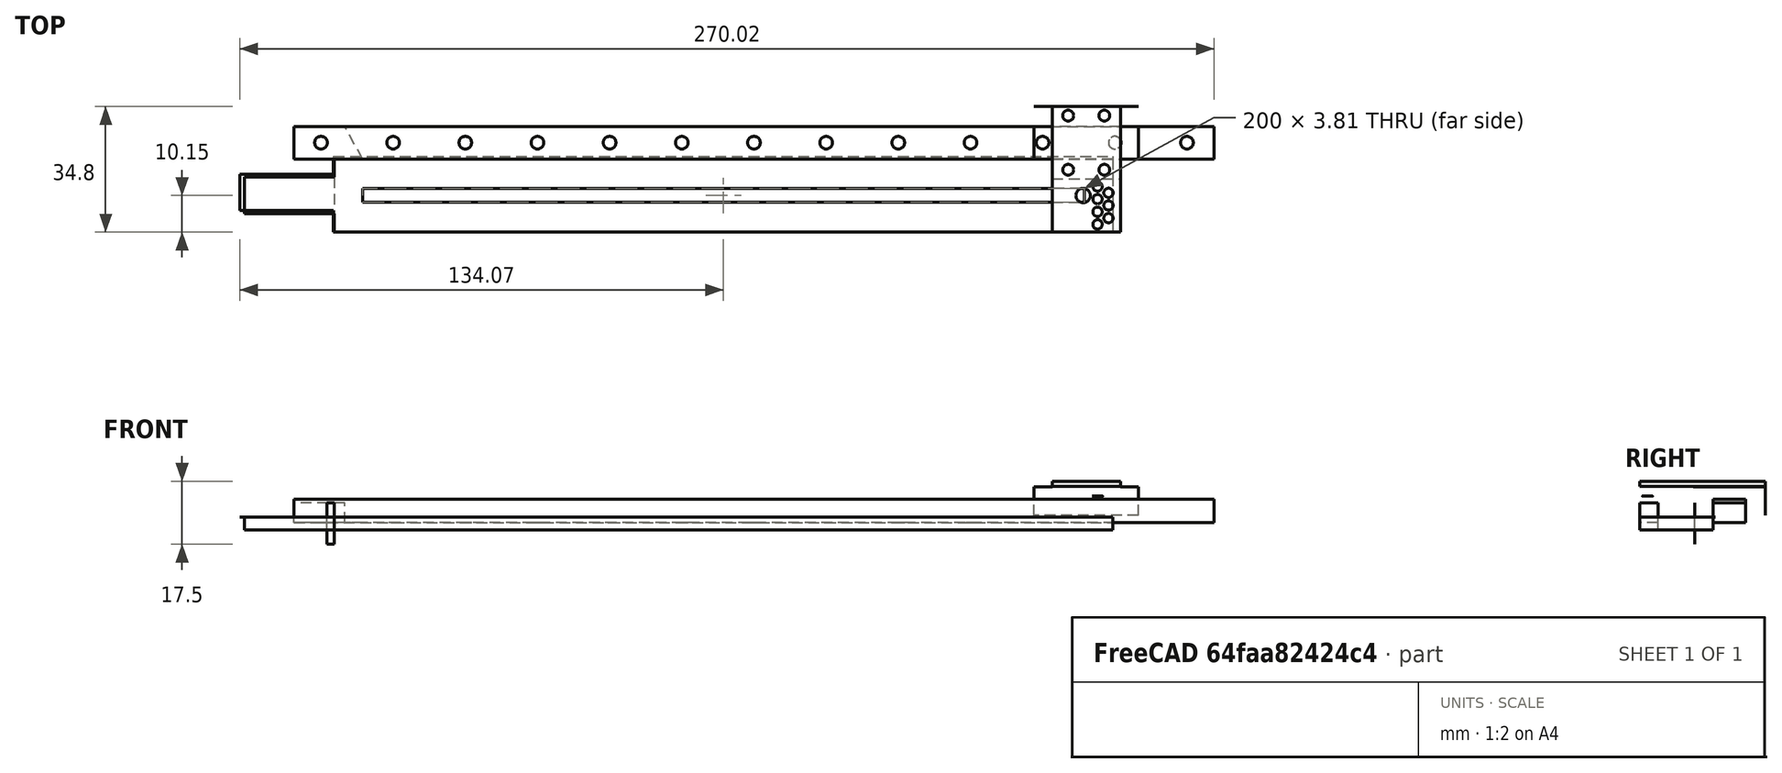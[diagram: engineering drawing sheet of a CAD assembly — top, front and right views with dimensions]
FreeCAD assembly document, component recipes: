
FREECAD ASSEMBLY — COMPONENT RECIPES ("v9")

This assembly document has 13 components, labeled P0..P12 below (a component is one placed body or linked part). 9 of them carry a construction recipe — the FreeCAD feature program that regenerates the part from scratch, quoted from this document or its linked companion documents; the rest are supplied as boundary geometry only. No exploded tour is included for this assembly.
COMPONENT P0 — geometry summary ("Rail"; no construction recipe available for this part):
  bounding box: 255.0 x 9.0 x 6.5 mm
  tessellated surface: 6,356 triangles
  volume: 14105 mm^3 (95% of its bounding box)
  symmetry: 2-fold rotationally symmetric about the x axis; 2-fold rotationally symmetric about the y axis; 2-fold rotationally symmetric about the z axis; mirror-symmetric across its x mid-plane, y mid-plane, z mid-plane
COMPONENT P1 — recipe-attached ("Slide", a linked part whose construction recipe lives in a companion FreeCAD document of the same project; that document's serialized recipe follows).
Construction recipe (the companion document, serialized — sketch geometry with constraints, then the solid features built on it; lengths are millimeters unless a unit is written):

FCSTD DOCUMENT  (FreeCAD 0.21R33668 +26 (Git))
Label: mgn9c_slide
License: All rights reserved
LicenseURL: http://en.wikipedia.org/wiki/All_rights_reserved
objects: Sketcher::SketchObject×4, PartDesign::Pocket×3, App::Link×1, PartDesign::Pad×1, PartDesign::Body×1
note: 13 computed .brp shape members not serialized (recipe doc carries the construction recipe); baked Part::Feature solids carry a one-line shape summary decoded from their .brp
EXTERNAL_REF file=Datasheet.FCStd obj=Spreadsheet

FEATURE [App::Link] Link  label="mgn9c"
  LinkedObject = -> <external Datasheet.FCStd>#Spreadsheet
FEATURE [Sketcher::SketchObject] Sketch002
  FullyConstrained = true
  MapMode = 5
  Support = -> [XY_Plane001]
  expr: Constraints[10] = <<mgn9c>>.Dim_W
  expr: Constraints[9] = <<mgn9c>>.Dim_L
  sketch-geometry (4):
    g0: LineSegment StartX=0 StartY=0 StartZ=0 EndX=28.9 EndY=0 EndZ=0
    g1: LineSegment StartX=28.9 StartY=0 StartZ=0 EndX=28.9 EndY=20 EndZ=0
    g2: LineSegment StartX=28.9 StartY=20 StartZ=0 EndX=0 EndY=20 EndZ=0
    g3: LineSegment StartX=0 StartY=20 StartZ=0 EndX=0 EndY=0 EndZ=0
  constraints (11):
    c: Coincident(g0,g1)
    c: Coincident(g1,g2)
    c: Coincident(g2,g3)
    c: Coincident(g3,g0)
    c: Horizontal(g0)
    c: Horizontal(g2)
    c: Vertical(g1)
    c: Vertical(g3)
    c: Coincident(g0,g-1)
    c: DistanceX(g2,g2) = 28.9
    c: DistanceY(g1,g1) = 20
FEATURE [PartDesign::Pad] Pad001
  Direction = (0,0,1)
  Length = 8
  Length2 = 10
  Profile = -> Sketch002
  ReferenceAxis = -> Sketch002 [N_Axis]
  Type = 0
  expr: Length = <<mgn9c>>.Dim_H - <<mgn9c>>.Dim_H1
FEATURE [Sketcher::SketchObject] Sketch003
  ExternalGeometry = -> [Pad001]
  FullyConstrained = true
  MapMode = 5
  Placement = pos=(0,0,0) rot=(0.57735,-0.57735,-0.57735;2.0944rad)
  Support = -> [Pad001]
  expr: Constraints[10] = <<mgn9c>>.Dim_Hr - <<mgn9c>>.Dim_H1
  expr: Constraints[8] = <<mgn9c>>.Dim_N
  expr: Constraints[9] = <<mgn9c>>.Dim_N
  sketch-geometry (4):
    g0: LineSegment StartX=-14.5 StartY=0 StartZ=0 EndX=-5.5 EndY=0 EndZ=0
    g1: LineSegment StartX=-5.5 StartY=0 StartZ=0 EndX=-5.5 EndY=4.5 EndZ=0
    g2: LineSegment StartX=-5.5 StartY=4.5 StartZ=0 EndX=-14.5 EndY=4.5 EndZ=0
    g3: LineSegment StartX=-14.5 StartY=4.5 StartZ=0 EndX=-14.5 EndY=0 EndZ=0
  constraints (12):
    c: Coincident(g0,g1)
    c: Coincident(g1,g2)
    c: Coincident(g2,g3)
    c: Coincident(g3,g0)
    c: Horizontal(g0)
    c: Horizontal(g2)
    c: Vertical(g1)
    c: Vertical(g3)
    c: DistanceX(g-5,g0) = 5.5
    c: DistanceX(g0,g-6) = 5.5
    c: DistanceY(g1,g1) = 4.5
    c: PointOnObject(g0,g-5)
FEATURE [PartDesign::Pocket] Pocket001
  BaseFeature = -> Pad001
  Direction = (1,0,0)
  Length = 28.9
  Length2 = 5
  Profile = -> Sketch003
  ReferenceAxis = -> Sketch003 [N_Axis]
  Type = 0
  expr: Length = <<mgn9c>>.Dim_L
FEATURE [Sketcher::SketchObject] Sketch004
  ExternalGeometry = -> [Pocket001]
  FullyConstrained = true
  MapMode = 5
  Placement = pos=(0,0,8) rot=(0,0,1;0rad)
  Support = -> [Pocket001]
  expr: Constraints[17] = 3
  expr: Constraints[18] = 3
  expr: Constraints[19] = 3
  expr: Constraints[20] = 3
  expr: Constraints[8] = <<mgn9c>>.Dim_C
  expr: Constraints[9] = <<mgn9c>>.Dim_B
  sketch-geometry (9):
    g0: LineSegment StartX=9.45 StartY=17.5 StartZ=0 EndX=19.45 EndY=17.5 EndZ=0
    g1: LineSegment StartX=19.45 StartY=17.5 StartZ=0 EndX=19.45 EndY=2.5 EndZ=0
    g2: LineSegment StartX=19.45 StartY=2.5 StartZ=0 EndX=9.45 EndY=2.5 EndZ=0
    g3: LineSegment StartX=9.45 StartY=2.5 StartZ=0 EndX=9.45 EndY=17.5 EndZ=0
    g4: GeomPoint X=14.45 Y=10 Z=0
    g5: Circle CenterX=9.45 CenterY=17.5 CenterZ=0 NormalX=0 NormalY=0 NormalZ=1 AngleXU=0 Radius=1.5
    g6: Circle CenterX=19.45 CenterY=17.5 CenterZ=0 NormalX=0 NormalY=0 NormalZ=1 AngleXU=0 Radius=1.5
    g7: Circle CenterX=19.45 CenterY=2.5 CenterZ=0 NormalX=0 NormalY=0 NormalZ=1 AngleXU=0 Radius=1.5
    g8: Circle CenterX=9.45 CenterY=2.5 CenterZ=0 NormalX=0 NormalY=0 NormalZ=1 AngleXU=0 Radius=1.5
  constraints (21):
    c: Coincident(g0,g1)
    c: Coincident(g1,g2)
    c: Coincident(g2,g3)
    c: Coincident(g3,g0)
    c: Horizontal(g0)
    c: Horizontal(g2)
    c: Vertical(g1)
    c: Vertical(g3)
    c: DistanceX(g0,g0) = 10
    c: DistanceY(g1,g1) = 15
    c: DistanceY(g-4,g2) = 2.5
    c: Symmetric(g-3,g-4,g4)
    c: Symmetric(g1,g0,g4)
    c: Coincident(g5,g0)
    c: Coincident(g6,g0)
    c: Coincident(g7,g1)
    c: Coincident(g8,g2)
    c: Diameter(g8) = 3
    c: Diameter(g7) = 3
    c: Diameter(g6) = 3
    c: Diameter(g5) = 3
FEATURE [PartDesign::Pocket] Pocket002
  BaseFeature = -> Pocket001
  Direction = (0,0,-1)
  Length = 3
  Length2 = 5
  Profile = -> Sketch004
  ReferenceAxis = -> Sketch004 [N_Axis]
  Type = 0
FEATURE [Sketcher::SketchObject] Sketch005
  ExternalGeometry = -> [Pocket002]
  FullyConstrained = true
  MapMode = 5
  Placement = pos=(0,0,8) rot=(0,0,1;0rad)
  Support = -> [Pocket002]
  expr: Constraints[19] = <<mgn9c>>.Dim_L1
  sketch-geometry (9):
    g0: LineSegment StartX=0 StartY=20 StartZ=0 EndX=5 EndY=20 EndZ=0
    g1: LineSegment StartX=5 StartY=20 StartZ=0 EndX=5 EndY=0 EndZ=0
    g2: LineSegment StartX=5 StartY=0 StartZ=0 EndX=0 EndY=0 EndZ=0
    g3: LineSegment StartX=0 StartY=0 StartZ=0 EndX=0 EndY=20 EndZ=0
    g4: LineSegment StartX=28.9 StartY=0 StartZ=0 EndX=23.9 EndY=0 EndZ=0
    g5: LineSegment StartX=23.9 StartY=0 StartZ=0 EndX=23.9 EndY=20 EndZ=0
    g6: LineSegment StartX=23.9 StartY=20 StartZ=0 EndX=28.9 EndY=20 EndZ=0
    g7: LineSegment StartX=28.9 StartY=20 StartZ=0 EndX=28.9 EndY=0 EndZ=0
    g8: GeomPoint X=14.45 Y=0 Z=0
  constraints (22):
    c: Coincident(g0,g1)
    c: Coincident(g1,g2)
    c: Coincident(g2,g3)
    c: Coincident(g3,g0)
    c: Horizontal(g0)
    c: Horizontal(g2)
    c: Vertical(g1)
    c: Vertical(g3)
    c: Coincident(g0,g-3)
    c: PointOnObject(g1,g-1)
    c: Coincident(g4,g5)
    c: Coincident(g5,g6)
    c: Coincident(g6,g7)
    c: Coincident(g7,g4)
    c: Horizontal(g6)
    c: Vertical(g5)
    c: Vertical(g7)
    c: Symmetric(g2,g-4,g8)
    c: Symmetric(g4,g1,g8)
    c: DistanceX(g1,g4) = 18.9
    c: PointOnObject(g5,g-5)
    c: Coincident(g4,g-4)
FEATURE [PartDesign::Pocket] Pocket003
  BaseFeature = -> Pocket002
  Direction = (0,0,-1)
  Length = 0.1
  Length2 = 5
  Profile = -> Sketch005
  ReferenceAxis = -> Sketch005 [N_Axis]
  Type = 0
FEATURE [PartDesign::Body] Body001  label="Slide"
  Group = -> [Sketch002,Pad001,Sketch003,Pocket001,Sketch004,Pocket002,Sketch005,Pocket003]
  Origin = -> Origin001
  Tip = -> Pocket003
COMPONENT P2 — geometry summary ("MP1_L_0200_103_5_ST"; no construction recipe available for this part):
  bounding box: 240.7 x 20.3 x 3.5 mm
  tessellated surface: 48 triangles
  volume: 13555 mm^3 (79% of its bounding box)
  symmetry: 2-fold rotationally symmetric about the x axis; mirror-symmetric across its y mid-plane, z mid-plane
COMPONENT P3 — geometry summary ("SlideConnector"; no construction recipe available for this part):
  bounding box: 34.8 x 18.9 x 9.5 mm
  tessellated surface: 4,764 triangles
  volume: 1826 mm^3 (29% of its bounding box)
COMPONENT P4 — recipe-attached ("7945", a linked part whose construction recipe lives in a companion FreeCAD document of the same project; that document's serialized recipe follows).
Construction recipe (the companion document, serialized — sketch geometry with constraints, then the solid features built on it; lengths are millimeters unless a unit is written):

FCSTD DOCUMENT  (FreeCAD 0.21R33668 +26 (Git))
Label: OmniballConnector_7945
License: All rights reserved
LicenseURL: http://en.wikipedia.org/wiki/All_rights_reserved
objects: Sketcher::SketchObject×4, PartDesign::Pad×3, PartDesign::Revolution×1, PartDesign::Body×1
note: 13 computed .brp shape members not serialized (recipe doc carries the construction recipe); baked Part::Feature solids carry a one-line shape summary decoded from their .brp

FEATURE [Sketcher::SketchObject] Sketch
  FullyConstrained = true
  MapMode = 5
  Support = -> [XY_Plane]
  expr: .Constraints.TopRad = 0.118 in
  sketch-geometry (1):
    g0: Circle CenterX=0 CenterY=0 CenterZ=0 NormalX=0 NormalY=0 NormalZ=1 AngleXU=0 Radius=1.4986
  constraints (2):
    c: Coincident(g0,g-1)
    c: Diameter(g0) = 2.9972  'TopRad'
FEATURE [PartDesign::Pad] Pad
  Direction = (0,0,1)
  Length = 0.762
  Length2 = 10
  Profile = -> Sketch
  ReferenceAxis = -> Sketch [N_Axis]
  Type = 0
  expr: Length = 0.03 in
FEATURE [Sketcher::SketchObject] Sketch001
  FullyConstrained = true
  MapMode = 5
  Placement = pos=(0,0,0.762) rot=(0,0,1;0rad)
  Support = -> [Pad]
  expr: Constraints[1] = 0.107 in
  sketch-geometry (1):
    g0: Circle CenterX=0 CenterY=0 CenterZ=0 NormalX=0 NormalY=0 NormalZ=1 AngleXU=0 Radius=1.3589
  constraints (2):
    c: Coincident(g0,g-1)
    c: Diameter(g0) = 2.7178
FEATURE [PartDesign::Pad] Pad001
  BaseFeature = -> Pad
  Direction = (0,0,1)
  Length = 0.7112
  Length2 = 10
  Profile = -> Sketch001
  ReferenceAxis = -> Sketch001 [N_Axis]
  Type = 0
  expr: Length = 0.028 in
FEATURE [Sketcher::SketchObject] Sketch002
  FullyConstrained = true
  MapMode = 5
  Placement = pos=(0,0,1.4732) rot=(0,0,1;0rad)
  Support = -> [Pad001]
  expr: .Constraints.Smallest_Radius = 0.102 in
  sketch-geometry (1):
    g0: Circle CenterX=0 CenterY=0 CenterZ=0 NormalX=0 NormalY=0 NormalZ=1 AngleXU=0 Radius=1.2954
  constraints (2):
    c: Coincident(g0,g-1)
    c: Diameter(g0) = 2.5908  'Smallest_Radius'
FEATURE [PartDesign::Pad] Pad002
  BaseFeature = -> Pad001
  Direction = (0,0,1)
  Length = 4.5212
  Length2 = 10
  Profile = -> Sketch002
  ReferenceAxis = -> Sketch002 [N_Axis]
  Type = 0
  expr: Length = 0.236 in - 0.058 in
FEATURE [Sketcher::SketchObject] Sketch003
  FullyConstrained = true
  MapMode = 5
  Placement = pos=(0,0,5.9944) rot=(0,0,1;0rad)
  Support = -> [Pad002]
  expr: Constraints[3] = 0.091 in / 2
  sketch-geometry (2):
    g0: ArcOfCircle CenterX=0 CenterY=0 CenterZ=0 NormalX=0 NormalY=0 NormalZ=1 AngleXU=0 Radius=1.1557 StartAngle=4.71239 EndAngle=7.85398
    g1: LineSegment StartX=4e-16 StartY=1.1557 StartZ=0 EndX=-2e-16 EndY=-1.1557 EndZ=0
  constraints (6):
    c: Coincident(g0,g-1)
    c: PointOnObject(g0,g-2)
    c: PointOnObject(g0,g-2)
    c: Radius(g0) = 1.1557
    c: Coincident(g1,g0)
    c: Coincident(g1,g0)
FEATURE [PartDesign::Revolution] Revolution
  Angle = 180
  Axis = (0,1,0)
  Base = (0,0,5.9944)
  BaseFeature = -> Pad002
  Profile = -> Sketch003
  ReferenceAxis = -> Sketch003 [V_Axis]
  Reversed = true
FEATURE [PartDesign::Body] Body  label="7945"
  Group = -> [Sketch,Pad,Sketch001,Pad001,Sketch002,Pad002,Sketch003,Revolution]
  Origin = -> Origin
  Tip = -> Revolution
COMPONENT P5 — same part as P4; its construction recipe is shown at P4.
COMPONENT P6 — same part as P4; its construction recipe is shown at P4.
COMPONENT P7 — same part as P4; its construction recipe is shown at P4.
COMPONENT P8 — same part as P4; its construction recipe is shown at P4.
COMPONENT P9 — same part as P4; its construction recipe is shown at P4.
COMPONENT P10 — same part as P4; its construction recipe is shown at P4.
COMPONENT P11 — recipe-attached ("FlexBoard", a linked part whose construction recipe lives in a companion FreeCAD document of the same project; that document's serialized recipe follows).
Construction recipe (the companion document, serialized — sketch geometry with constraints, then the solid features built on it; lengths are millimeters unless a unit is written):

FCSTD DOCUMENT  (FreeCAD 0.21R33668 +26 (Git))
Label: FlexBoard_CAD
License: All rights reserved
LicenseURL: http://en.wikipedia.org/wiki/All_rights_reserved
objects: Part::Feature×5, App::Part×4, PartDesign::CoordinateSystem×1, Sketcher::SketchObject×1
note: 7 computed .brp shape members not serialized (recipe doc carries the construction recipe); baked Part::Feature solids carry a one-line shape summary decoded from their .brp

FEATURE [PartDesign::CoordinateSystem] Local_CS_2da8
  AttacherType = Attacher::AttachEngine3D
  MapMode = 2
  Support = -> [X_Axis001]
FEATURE [Part::Feature] Pcb_2da8
  Placement = pos=(-80.4,100.6,0) rot=(0,0,1;0rad)
  shape: bbox 242 x 21 x 0.115 mm, 10 faces (baked)
FEATURE [Sketcher::SketchObject] PCB_Sketch_2da8
  FullyConstrained = false
  sketch-geometry (8):
    g0: LineSegment StartX=-14.4 StartY=9.6 StartZ=0 EndX=201.6 EndY=9.6 EndZ=0
    g1: LineSegment StartX=-14.4 StartY=-5.4 StartZ=0 EndX=-14.4 EndY=-11.4 EndZ=0
    g2: LineSegment StartX=-40.4 StartY=-5.4 StartZ=0 EndX=-14.4 EndY=-5.4 EndZ=0
    g3: LineSegment StartX=-14.4 StartY=4.6 StartZ=0 EndX=-40.4 EndY=4.6 EndZ=0
    g4: LineSegment StartX=-14.4 StartY=9.6 StartZ=0 EndX=-14.4 EndY=4.6 EndZ=0
    g5: LineSegment StartX=-40.4 StartY=4.6 StartZ=0 EndX=-40.4 EndY=-5.4 EndZ=0
    g6: LineSegment StartX=201.6 StartY=-11.4 StartZ=0 EndX=-14.4 EndY=-11.4 EndZ=0
    g7: LineSegment StartX=201.6 StartY=9.6 StartZ=0 EndX=201.6 EndY=-11.4 EndZ=0
  constraints (8):
    c: Coincident(g2,g5)
    c: Coincident(g3,g5)
    c: Coincident(g1,g6)
    c: Coincident(g1,g2)
    c: Coincident(g3,g4)
    c: Coincident(g0,g4)
    c: Coincident(g6,g7)
    c: Coincident(g0,g7)
FEATURE [Part::Feature] Shape  label="J1_PinHeader_1x07_P100mm_Vertical_SMD_Pin1Right_2c072f5cbf80"
  Placement = pos=(-35.275,-0.4,0) rot=(0,0,1;0rad)
  shape: bbox 2.5 x 7 x 4 mm, 193 faces (baked)
FEATURE [App::Part] Top_2da8
  Group = -> [Shape]
  Origin = -> Origin003
FEATURE [App::Part] Step_Models_2da8
  Group = -> [Top_2da8]
  Origin = -> Origin002
FEATURE [Part::Feature] track_area001  label="topTracks_2da8"
  Placement = pos=(-80.4,100.6,0.01) rot=(0,0,1;0rad)
  shape: bbox 37 x 12.25 x 2e-07 mm, 7 faces, 0 solids (baked)
FEATURE [Part::Feature] zones_area001  label="topZones_2da8"
  Placement = pos=(-80.4,100.6,0.01) rot=(0,0,1;0rad)
  shape: bbox 204.1 x 11.55 x 2e-07 mm, 7 faces, 0 solids (baked)
FEATURE [Part::Feature] topPads_2da8_  label="topPads_2da8_cut"
  Placement = pos=(0,0,0.02) rot=(0,0,1;0rad)
  shape: bbox 3.5 x 6.6 x 2e-07 mm, 7 faces, 0 solids (baked)
FEATURE [App::Part] Board_Geoms_2da8
  Group = -> [Pcb_2da8,PCB_Sketch_2da8,topPads_2da8_,track_area001,zones_area001]
  Origin = -> Origin
FEATURE [App::Part] Board_2da8  label="FlexBoard"
  Group = -> [Local_CS_2da8,Board_Geoms_2da8,Step_Models_2da8]
  Origin = -> Origin001
COMPONENT P12 — geometry summary ("BaseMagentoPot"; no construction recipe available for this part):
  bounding box: 33.3 x 21.0 x 11.5 mm
  tessellated surface: 1,084 triangles
  volume: 2699 mm^3 (33% of its bounding box)
PROVENANCE & LICENSES
A FreeCAD (.FCStd) document from a public repository crawl; recipes are the document's own serialized feature recipes (and, for linked parts, companion documents' recipes).
License: as declared in the source repository (recorded in the dataset sidecar).
